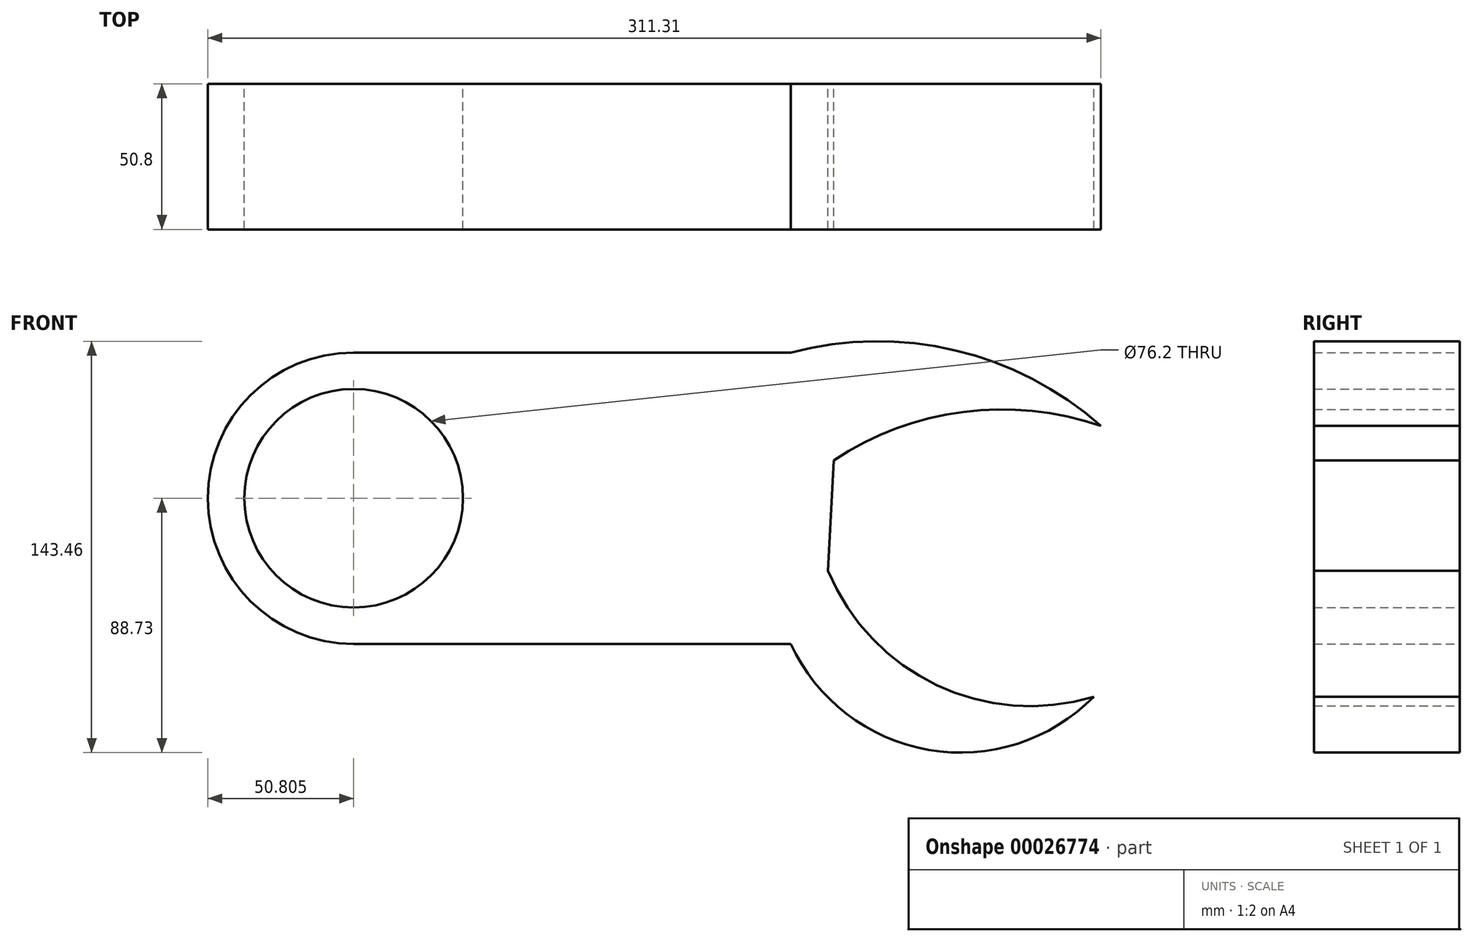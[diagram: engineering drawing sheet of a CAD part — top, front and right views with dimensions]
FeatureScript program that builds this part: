
annotation { "Feature Type Name" : "Feature", "Feature Type Description" : "" }
export const myFeature = defineFeature(function(context is Context, id is Id, definition is map)
    precondition{}
    {
        {
            var Q0;
            Q0=qCreatedBy(makeId("Front.planeOp"),FACE);
            var sketch = newSketch(context, id + "F0", { "sketchPlane" : qUnion([Q0])});
            skLineSegment(sketch, "E0.bottom", {"start": v(-81.25, -50.8) * mm, "end": v(71.15, -50.8) * mm});
            skLineSegment(sketch, "E0.top", {"start": v(-81.25, 50.8) * mm, "end": v(71.15, 50.8) * mm});
            skArc(sketch, "E1", {"start": v(-81.25, 50.8) * mm, "mid": v(-132.05, 0) * mm, "end": v(-81.25, -50.8) * mm});
            skCircle(sketch, "E2", {"center": v(-81.25, 0) * mm, "radius": 38.1 * mm});
            skPoint(sketch, "E3.center.orphan", {"position": v(71.15, 0) * mm});
            skArc(sketch, "E4", {"start": v(179.26, 25.2) * mm, "mid": v(128.42, 51.57) * mm, "end": v(71.15, 50.8) * mm});
            skArc(sketch, "E5", {"start": v(179.26, 25.2) * mm, "mid": v(131.28, 30.06) * mm, "end": v(86.1, 13.21) * mm});
            skArc(sketch, "E6", {"start": v(71.15, -50.8) * mm, "mid": v(119.12, -87.76) * mm, "end": v(176.77, -69.21) * mm});
            skArc(sketch, "E7", {"start": v(84.14, -25.35) * mm, "mid": v(122, -65.14) * mm, "end": v(176.77, -69.21) * mm});
            skLineSegment(sketch, "E8", {"start": v(86.1, 13.21) * mm, "end": v(84.14, -25.35) * mm});
            skSolve(sketch);
        }
        {
            var Q0;
            Q0=makeQuery(id+"F0.imprint","IMPRINT",FACE,{"disambiguationData":[TD([[makeQuery(id+"F0.imprint","IMPRINT",EDGE,{"derivedFrom":sQuery(id+"F0.wireOp",EDGE,"E0.bottom")}),1.0]])]});
            extrude(context, id + "F1", {"entities" : qUnion([Q0]), "depth" : 50.8 * mm});
        }
    });
